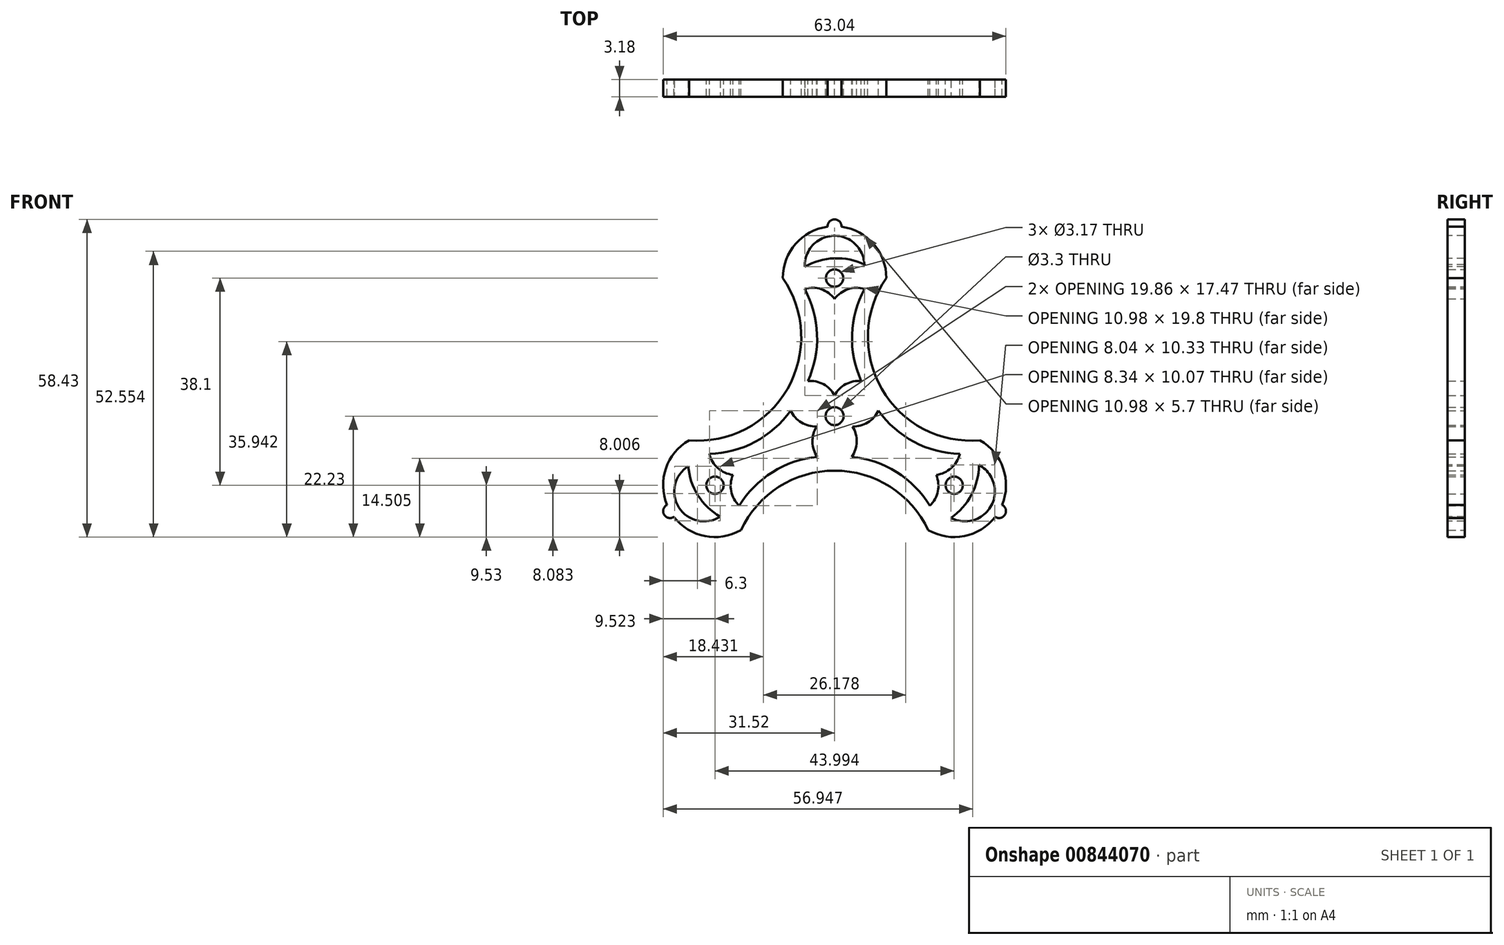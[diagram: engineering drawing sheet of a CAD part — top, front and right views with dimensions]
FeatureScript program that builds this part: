
annotation { "Feature Type Name" : "Feature", "Feature Type Description" : "" }
export const myFeature = defineFeature(function(context is Context, id is Id, definition is map)
    precondition{}
    {
        {
            var Q0;
            Q0=qCreatedBy(makeId("Front.planeOp"),FACE);
            var sketch = newSketch(context, id + "F0", { "sketchPlane" : qUnion([Q0])});
            skCircle(sketch, "E0", {"center": v(0, 0) * mm, "radius": 1.65 * mm});
            skCircle(sketch, "E1", {"center": v(0, 25.4) * mm, "radius": 1.59 * mm});
            skCircle(sketch, "E2", {"center": v(22, -12.7) * mm, "radius": 1.59 * mm});
            skCircle(sketch, "E3", {"center": v(-22, -12.7) * mm, "radius": 1.59 * mm});
            skArc(sketch, "E4", {"start": v(9.53, 25.4) * mm, "mid": v(7.17, 31.67) * mm, "end": v(1.27, 34.84) * mm});
            skArc(sketch, "E5", {"start": v(17.23, -20.95) * mm, "mid": v(23.84, -22.04) * mm, "end": v(29.54, -18.52) * mm});
            skArc(sketch, "E6", {"start": v(17.23, -20.95) * mm, "mid": v(0, -10.02) * mm, "end": v(-17.23, -20.95) * mm});
            skArc(sketch, "E7", {"start": v(-26.76, -4.45) * mm, "mid": v(-8.67, 5) * mm, "end": v(-9.53, 25.4) * mm});
            skArc(sketch, "E8", {"start": v(9.52, 25.4) * mm, "mid": v(8.67, 5) * mm, "end": v(26.76, -4.45) * mm});
            skArc(sketch, "E9.trimOffspring", {"start": v(-26.76, -4.45) * mm, "mid": v(-31.01, -9.63) * mm, "end": v(-30.8, -16.32) * mm});
            skPoint(sketch, "E10.orphan", {"position": v(44, 25.4) * mm});
            skPoint(sketch, "E11.orphan", {"position": v(-44, 25.4) * mm});
            skPoint(sketch, "E12.orphan", {"position": v(0, -50.8) * mm});
            skArc(sketch, "E13", {"start": v(-4.9, 6.48) * mm, "mid": v(-3.21, 15.01) * mm, "end": v(-5.5, 23.41) * mm});
            skArc(sketch, "E14", {"start": v(0, 21.59) * mm, "mid": v(-2.46, 23.35) * mm, "end": v(-5.5, 23.41) * mm});
            skArc(sketch, "E15.MirrorCS", {"start": v(0, 21.59) * mm, "mid": v(2.46, 23.35) * mm, "end": v(5.5, 23.41) * mm});
            skArc(sketch, "E16.MirrorCS", {"start": v(4.9, 6.48) * mm, "mid": v(3.21, 15.01) * mm, "end": v(5.5, 23.41) * mm});
            skArc(sketch, "E17", {"start": v(0, 3.81) * mm, "mid": v(-2.05, 5.88) * mm, "end": v(-4.9, 6.48) * mm});
            skPoint(sketch, "E18.start.orphan", {"position": v(-6.7, 3.35) * mm});
            skArc(sketch, "E19", {"start": v(4.9, 6.48) * mm, "mid": v(2.05, 5.88) * mm, "end": v(0, 3.81) * mm});
            skPoint(sketch, "E20.MirrorCS.start.orphan", {"position": v(6.7, 3.35) * mm});
            skArc(sketch, "E21.1.0", {"start": v(-8.06, 1.01) * mm, "mid": v(-14.6, -4.72) * mm, "end": v(-23.02, -6.95) * mm});
            skArc(sketch, "E21.1.1", {"start": v(-18.7, -10.8) * mm, "mid": v(-21.46, -9.54) * mm, "end": v(-23.02, -6.95) * mm});
            skArc(sketch, "E21.1.2", {"start": v(-18.7, -10.8) * mm, "mid": v(-19, -13.81) * mm, "end": v(-17.53, -16.46) * mm});
            skArc(sketch, "E21.1.3", {"start": v(-3.16, -7.49) * mm, "mid": v(-11.4, -10.29) * mm, "end": v(-17.53, -16.46) * mm});
            skArc(sketch, "E21.1.4", {"start": v(-3.3, -1.9) * mm, "mid": v(-4.06, -4.72) * mm, "end": v(-3.16, -7.49) * mm});
            skArc(sketch, "E21.1.5", {"start": v(-8.06, 1.01) * mm, "mid": v(-6.12, -1.16) * mm, "end": v(-3.3, -1.9) * mm});
            skArc(sketch, "E21.2.0", {"start": v(3.16, -7.49) * mm, "mid": v(11.4, -10.29) * mm, "end": v(17.53, -16.46) * mm});
            skArc(sketch, "E21.2.1", {"start": v(18.7, -10.8) * mm, "mid": v(19, -13.81) * mm, "end": v(17.53, -16.46) * mm});
            skArc(sketch, "E21.2.2", {"start": v(18.7, -10.8) * mm, "mid": v(21.46, -9.54) * mm, "end": v(23.02, -6.95) * mm});
            skArc(sketch, "E21.2.3", {"start": v(8.06, 1.01) * mm, "mid": v(14.6, -4.72) * mm, "end": v(23.02, -6.95) * mm});
            skArc(sketch, "E21.2.4", {"start": v(3.3, -1.9) * mm, "mid": v(6.12, -1.16) * mm, "end": v(8.06, 1.01) * mm});
            skArc(sketch, "E21.2.5", {"start": v(3.16, -7.49) * mm, "mid": v(4.06, -4.72) * mm, "end": v(3.3, -1.9) * mm});
            skArc(sketch, "E22", {"start": v(1.27, 34.84) * mm, "mid": v(0, 36.2) * mm, "end": v(-1.27, 34.84) * mm});
            skArc(sketch, "E23.trimOffspring", {"start": v(-1.27, 34.84) * mm, "mid": v(-7.17, 31.67) * mm, "end": v(-9.53, 25.4) * mm});
            skArc(sketch, "E24.1.0", {"start": v(-30.8, -16.32) * mm, "mid": v(-31.35, -18.1) * mm, "end": v(-29.54, -18.52) * mm});
            skArc(sketch, "E24.2.0", {"start": v(29.54, -18.52) * mm, "mid": v(31.35, -18.1) * mm, "end": v(30.8, -16.32) * mm});
            skArc(sketch, "E25.trimOffspring", {"start": v(30.8, -16.32) * mm, "mid": v(31.01, -9.63) * mm, "end": v(26.76, -4.45) * mm});
            skArc(sketch, "E26.trimOffspring", {"start": v(-29.54, -18.52) * mm, "mid": v(-23.84, -22.04) * mm, "end": v(-17.23, -20.95) * mm});
            skSolve(sketch);
        }
        {
            var Q0;
            Q0=makeQuery(id+"F0.imprint","IMPRINT",FACE,{"disambiguationData":[TD([[makeQuery(id+"F0.imprint","IMPRINT",EDGE,{"derivedFrom":sQuery(id+"F0.wireOp",EDGE,"E1")}),-1.0]])]});
            extrude(context, id + "F1", {"entities" : qUnion([Q0]), "depth" : 3.17 * mm, "offsetDistance" : 25.4 * mm});
        }
        {
            var Q0;
            Q0=makeQuery(id+"F1.opExtrude","CAP_FACE",FACE,{"disambiguationData":[OSD([sQuery(id+"F0.wireOp",EDGE,"E1"),sQuery(id+"F0.wireOp",EDGE,"E2"),sQuery(id+"F0.wireOp",EDGE,"E3"),sQuery(id+"F0.wireOp",EDGE,"E4"),sQuery(id+"F0.wireOp",EDGE,"E5"),sQuery(id+"F0.wireOp",EDGE,"E6"),sQuery(id+"F0.wireOp",EDGE,"E7"),sQuery(id+"F0.wireOp",EDGE,"E8"),sQuery(id+"F0.wireOp",EDGE,"E9.trimOffspring"),sQuery(id+"F0.wireOp",EDGE,"E13"),sQuery(id+"F0.wireOp",EDGE,"E14"),sQuery(id+"F0.wireOp",EDGE,"E15.MirrorCS"),sQuery(id+"F0.wireOp",EDGE,"E16.MirrorCS"),sQuery(id+"F0.wireOp",EDGE,"E17"),sQuery(id+"F0.wireOp",EDGE,"E19"),sQuery(id+"F0.wireOp",EDGE,"E0"),sQuery(id+"F0.wireOp",EDGE,"E21.1.0"),sQuery(id+"F0.wireOp",EDGE,"E21.1.1"),sQuery(id+"F0.wireOp",EDGE,"E21.1.2"),sQuery(id+"F0.wireOp",EDGE,"E21.1.3"),sQuery(id+"F0.wireOp",EDGE,"E21.1.4"),sQuery(id+"F0.wireOp",EDGE,"E21.1.5"),sQuery(id+"F0.wireOp",EDGE,"E21.2.0"),sQuery(id+"F0.wireOp",EDGE,"E21.2.1"),sQuery(id+"F0.wireOp",EDGE,"E21.2.2"),sQuery(id+"F0.wireOp",EDGE,"E21.2.3"),sQuery(id+"F0.wireOp",EDGE,"E21.2.4"),sQuery(id+"F0.wireOp",EDGE,"E21.2.5")])],"isStart":false});
            var sketch = newSketch(context, id + "F2", { "sketchPlane" : qUnion([Q0])});
            skArc(sketch, "E27", {"start": v(5.5, 27.9) * mm, "mid": v(-0.05, 29.04) * mm, "end": v(-5.5, 27.47) * mm});
            skArc(sketch, "E28", {"start": v(5.5, 27.9) * mm, "mid": v(-0.2, 33.17) * mm, "end": v(-5.5, 27.47) * mm});
            skArc(sketch, "E29.1.0", {"start": v(-26.9, -9.19) * mm, "mid": v(-25.12, -14.56) * mm, "end": v(-21.05, -18.5) * mm});
            skArc(sketch, "E29.1.1", {"start": v(-26.9, -9.19) * mm, "mid": v(-28.63, -16.77) * mm, "end": v(-21.05, -18.5) * mm});
            skArc(sketch, "E29.2.0", {"start": v(21.4, -18.7) * mm, "mid": v(25.17, -14.47) * mm, "end": v(26.54, -8.98) * mm});
            skArc(sketch, "E29.2.1", {"start": v(21.4, -18.7) * mm, "mid": v(28.83, -16.4) * mm, "end": v(26.54, -8.98) * mm});
            skPoint(sketch, "E29.center", {"position": v(0, 0) * mm});
            skSolve(sketch);
        }
        {
            var Q0;
            Q0=makeQuery(id+"F2.imprint","IMPRINT",FACE,{"disambiguationData":[TD([[makeQuery(id+"F2.imprint","IMPRINT",EDGE,{"derivedFrom":sQuery(id+"F2.wireOp",EDGE,"E27")}),-1.0]])]});
            var Q1;
            Q1=makeQuery(id+"F2.imprint","IMPRINT",FACE,{"disambiguationData":[TD([[makeQuery(id+"F2.imprint","IMPRINT",EDGE,{"derivedFrom":sQuery(id+"F2.wireOp",EDGE,"E29.1.0")}),-1.0]])]});
            var Q2;
            Q2=makeQuery(id+"F2.imprint","IMPRINT",FACE,{"disambiguationData":[TD([[makeQuery(id+"F2.imprint","IMPRINT",EDGE,{"derivedFrom":sQuery(id+"F2.wireOp",EDGE,"E29.2.0")}),-1.0]])]});
            extrude(context, id + "F3", {"entities" : qUnion([Q0, Q1, Q2]), "operationType" : NewBodyOperationType.REMOVE, "oppositeDirection" : true, "depth" : 25.4 * mm, "offsetDistance" : 25.4 * mm});
        }
    });
